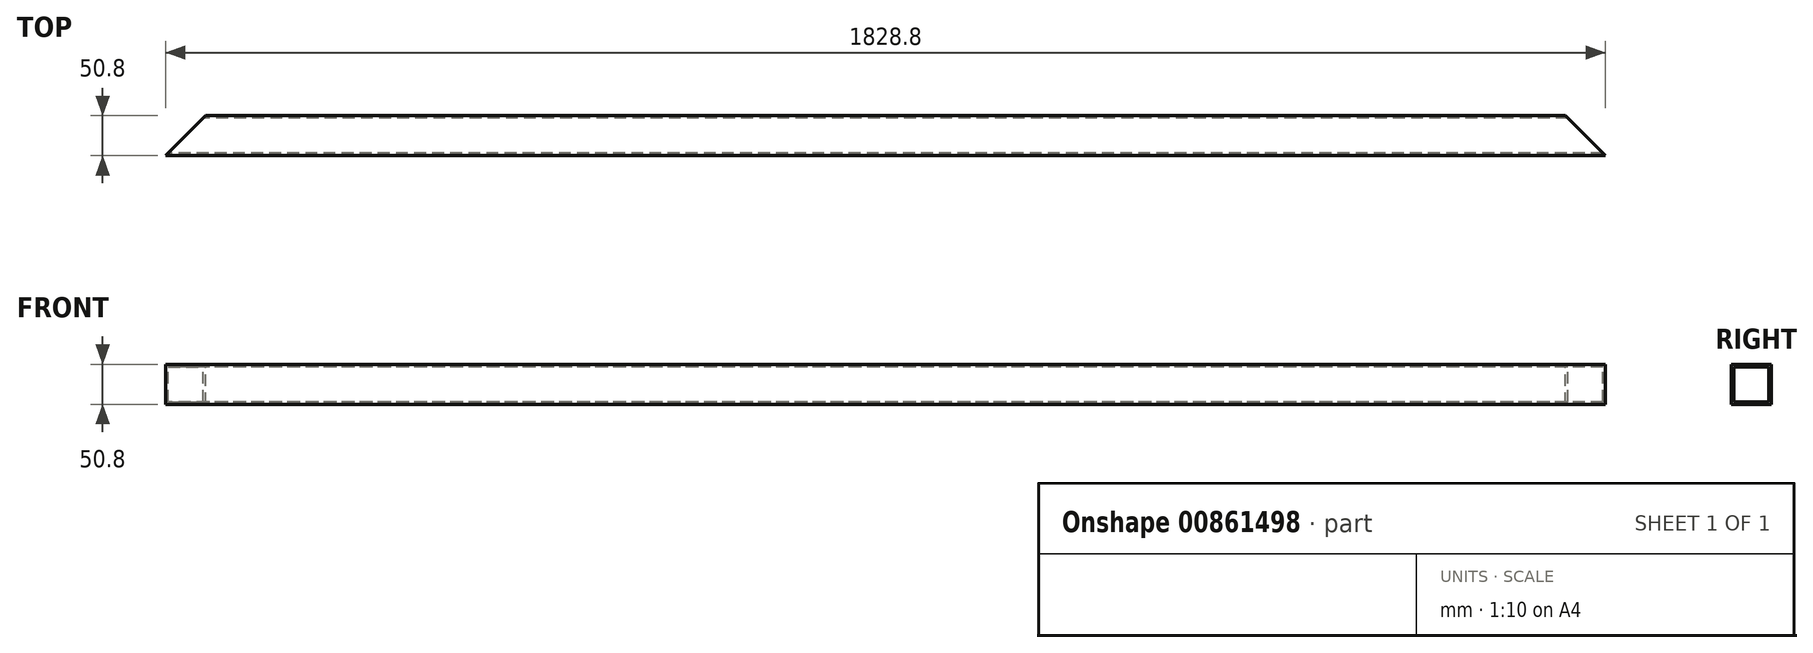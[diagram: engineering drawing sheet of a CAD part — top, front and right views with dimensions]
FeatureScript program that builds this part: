
annotation { "Feature Type Name" : "Feature", "Feature Type Description" : "" }
export const myFeature = defineFeature(function(context is Context, id is Id, definition is map)
    precondition{}
    {
        {
            var Q0;
            Q0=qCreatedBy(makeId("Right.planeOp"),FACE);
            var sketch = newSketch(context, id + "F0", { "sketchPlane" : qUnion([Q0])});
            skLineSegment(sketch, "E0.bottom", {"start": v(0, 0) * mm, "end": v(50.8, 0) * mm});
            skLineSegment(sketch, "E0.top", {"start": v(0, 50.8) * mm, "end": v(50.8, 50.8) * mm});
            skLineSegment(sketch, "E0.left", {"start": v(0, 0) * mm, "end": v(0, 50.8) * mm});
            skLineSegment(sketch, "E0.right", {"start": v(50.8, 0) * mm, "end": v(50.8, 50.8) * mm});
            skLineSegment(sketch, "E1.bottom", {"start": v(3.18, 3.18) * mm, "end": v(47.63, 3.18) * mm});
            skLineSegment(sketch, "E1.top", {"start": v(3.17, 47.63) * mm, "end": v(47.62, 47.63) * mm});
            skLineSegment(sketch, "E1.left", {"start": v(3.17, 3.18) * mm, "end": v(3.17, 47.63) * mm});
            skLineSegment(sketch, "E1.right", {"start": v(47.63, 3.18) * mm, "end": v(47.62, 47.63) * mm});
            skSolve(sketch);
        }
        {
            var Q0;
            Q0=makeQuery(id+"F0.imprint","IMPRINT",FACE,{"disambiguationData":[TD([[makeQuery(id+"F0.imprint","IMPRINT",EDGE,{"derivedFrom":sQuery(id+"F0.wireOp",EDGE,"E0.bottom")}),1.0]])]});
            extrude(context, id + "F1", {"entities" : qUnion([Q0]), "depth" : 1828.8 * mm, "offsetDistance" : 25.4 * mm});
        }
        {
            var Q0;
            Q0=makeQuery(id+"F1.opExtrude","SWEPT_FACE",FACE,{"disambiguationData":[OSD([sQuery(id+"F0.wireOp",EDGE,"E0.top")])]});
            var sketch = newSketch(context, id + "F2", { "sketchPlane" : qUnion([Q0])});
            skLineSegment(sketch, "E2", {"start": v(0, 0) * mm, "end": v(50.8, 50.8) * mm});
            skLineSegment(sketch, "E3", {"start": v(1828.8, 0) * mm, "end": v(1778, 50.8) * mm});
            skSolve(sketch);
        }
        {
            var Q0;
            {var subQ0=sQuery(id+"F2.wireOp",EDGE,"E2");Q0=makeQuery(id+"F2.imprint","IMPRINT",FACE,{"disambiguationData":[TD([[makeQuery(id+"F2.imprint","IMPRINT",EDGE,{"derivedFrom":subQ0}),1.0]])]});}
            var Q1;
            {var subQ0=sQuery(id+"F2.wireOp",EDGE,"E3");Q1=makeQuery(id+"F2.imprint","IMPRINT",FACE,{"disambiguationData":[TD([[makeQuery(id+"F2.imprint","IMPRINT",EDGE,{"derivedFrom":subQ0}),-1.0]])]});}
            extrude(context, id + "F3", {"entities" : qUnion([Q0, Q1]), "operationType" : NewBodyOperationType.REMOVE, "endBound" : BoundingType.THROUGH_ALL, "oppositeDirection" : true, "depth" : 25.4 * mm, "offsetDistance" : 25.4 * mm});
        }
    });
